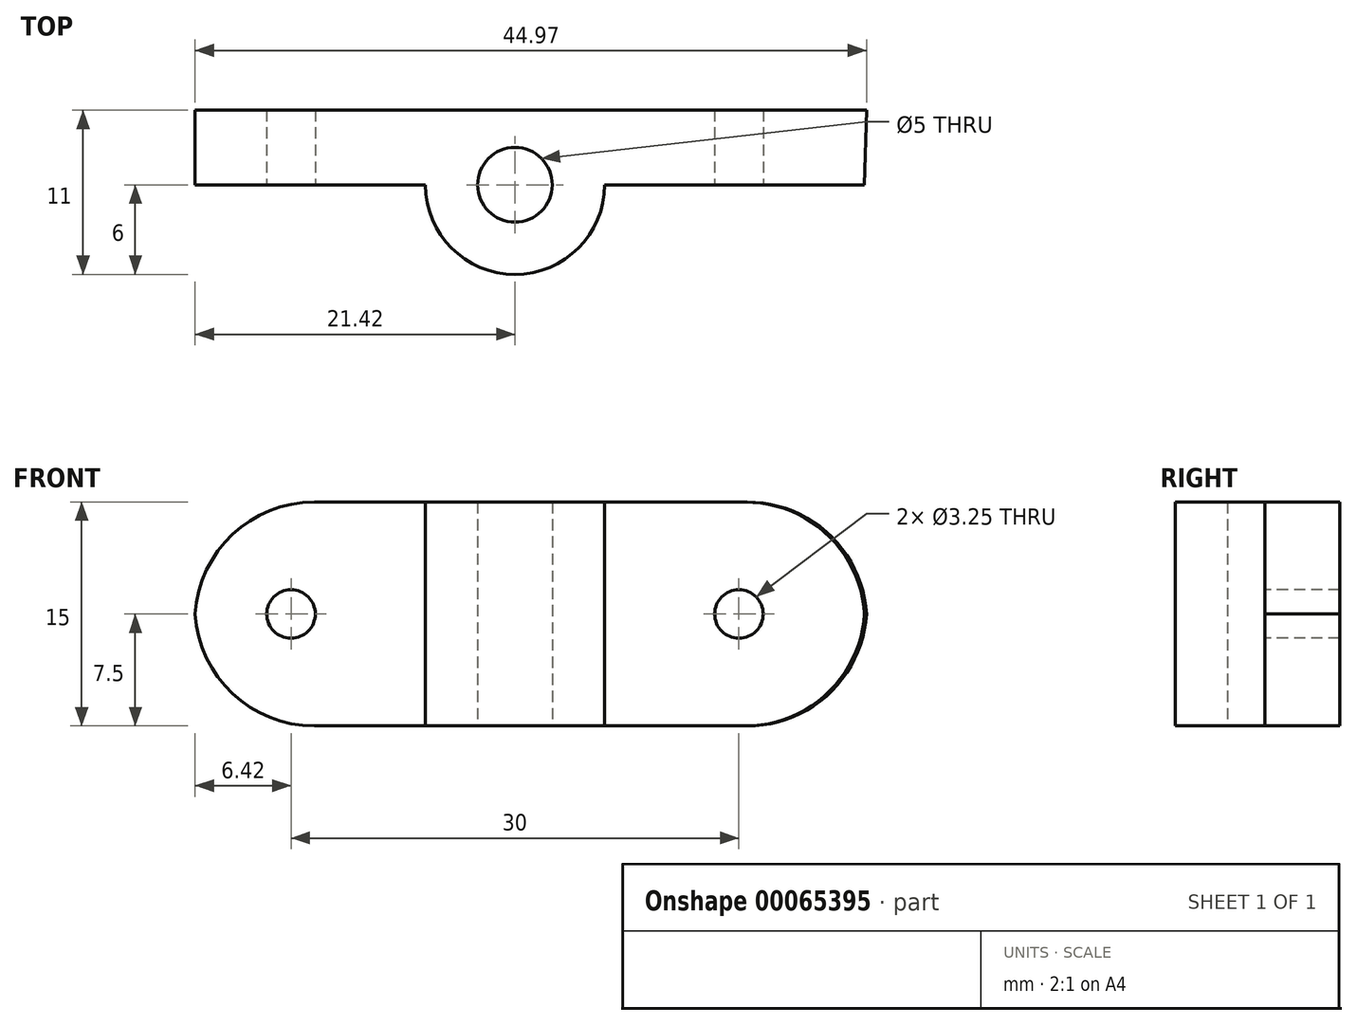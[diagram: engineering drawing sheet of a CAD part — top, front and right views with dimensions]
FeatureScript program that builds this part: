
annotation { "Feature Type Name" : "Feature", "Feature Type Description" : "" }
export const myFeature = defineFeature(function(context is Context, id is Id, definition is map)
    precondition{}
    {
        {
            var Q0;
            Q0=qCreatedBy(makeId("Top.planeOp"),FACE);
            var sketch = newSketch(context, id + "F0", { "sketchPlane" : qUnion([Q0])});
            skCircle(sketch, "E0", {"center": v(0, 0) * mm, "radius": 2.5 * mm});
            skCircle(sketch, "E1", {"center": v(0, 0) * mm, "radius": 6 * mm, "construction": true});
            skLineSegment(sketch, "E2", {"start": v(23.43, 0) * mm, "end": v(6, 0) * mm});
            skLineSegment(sketch, "E3", {"start": v(-6, 0) * mm, "end": v(-21.44, 0) * mm});
            skLineSegment(sketch, "E4", {"start": v(-21.44, 0) * mm, "end": v(-21.44, 5) * mm});
            skLineSegment(sketch, "E5", {"start": v(-21.44, 5) * mm, "end": v(23.56, 5) * mm});
            skLineSegment(sketch, "E6", {"start": v(23.56, 5) * mm, "end": v(23.43, 0) * mm});
            skArc(sketch, "E7", {"start": v(6, 0) * mm, "mid": v(0, -6) * mm, "end": v(-6, 0) * mm});
            skSolve(sketch);
        }
        {
            var Q0;
            Q0=makeQuery(id+"F0.imprint","IMPRINT",FACE,{"disambiguationData":[TD([[makeQuery(id+"F0.imprint","IMPRINT",EDGE,{"derivedFrom":sQuery(id+"F0.wireOp",EDGE,"E0")}),-1.0]])]});
            extrude(context, id + "F1", {"entities" : qUnion([Q0]), "depth" : 15 * mm});
        }
        {
            var Q0;
            Q0=makeQuery(id+"F1.opExtrude","SWEPT_FACE",FACE,{"disambiguationData":[OSD([sQuery(id+"F0.wireOp",EDGE,"E3")])]});
            var sketch = newSketch(context, id + "F2", { "sketchPlane" : qUnion([Q0])});
            skLineSegment(sketch, "E8", {"start": v(-21.44, 7.5) * mm, "end": v(24.47, 7.5) * mm, "construction": true});
            skPoint(sketch, "E9.centerSnap0", {"position": v(-13.72, 15) * mm});
            skCircle(sketch, "E10", {"center": v(15, 7.5) * mm, "radius": 1.75 * mm});
            skCircle(sketch, "E11", {"center": v(-15, 7.5) * mm, "radius": 1.75 * mm});
            skSolve(sketch);
        }
        {
            var Q0;
            Q0=sQuery(id+"F2.wireOp",VERTEX,"E11.center");
            var Q1;
            Q1=sQuery(id+"F2.wireOp",VERTEX,"E10.center");
            var Q2;
            Q2=makeQuery(id+"F1.opExtrude","SWEPT_BODY",BODY,{"disambiguationData":[OSD([sQuery(id+"F0.wireOp",EDGE,"E0"),sQuery(id+"F0.wireOp",EDGE,"E2"),sQuery(id+"F0.wireOp",EDGE,"E3"),sQuery(id+"F0.wireOp",EDGE,"E4"),sQuery(id+"F0.wireOp",EDGE,"E5"),sQuery(id+"F0.wireOp",EDGE,"E6"),sQuery(id+"F0.wireOp",EDGE,"E7")])]});
            hole(context, id + "F3", {"style" : HoleStyle.SIMPLE, "holeDiameter" : 3.25 * mm, "endStyle" : HoleEndStyle.THROUGH, "locations" : qUnion([Q0, Q1]), "scope" : qUnion([Q2])});
        }
        {
            var Q0;
            Q0=makeQuery(id+"F1.opExtrude","CAP_EDGE",EDGE,{"disambiguationData":[OSD([sQuery(id+"F0.wireOp",EDGE,"E4")])],"isStart":false});
            var Q1;
            Q1=makeQuery(id+"F1.opExtrude","CAP_EDGE",EDGE,{"disambiguationData":[OSD([sQuery(id+"F0.wireOp",EDGE,"E4")])],"isStart":true});
            var Q2;
            Q2=makeQuery(id+"F1.opExtrude","CAP_EDGE",EDGE,{"disambiguationData":[OSD([sQuery(id+"F0.wireOp",EDGE,"E6")])],"isStart":false});
            var Q3;
            Q3=makeQuery(id+"F1.opExtrude","CAP_EDGE",EDGE,{"disambiguationData":[OSD([sQuery(id+"F0.wireOp",EDGE,"E6")])],"isStart":true});
            fillet(context, id + "F4", {"entities" : qUnion([Q0, Q1, Q2, Q3]), "radius" : 8 * mm, "tangentPropagation" : true, "allowEdgeOverflow" : false});
        }
    });
